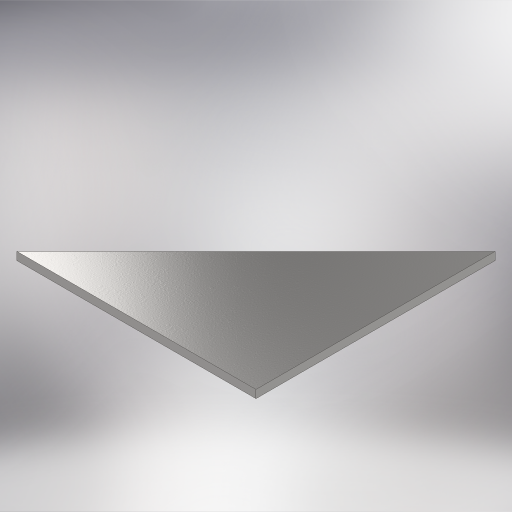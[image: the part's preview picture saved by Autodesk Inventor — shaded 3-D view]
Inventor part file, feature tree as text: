
AUTODESK INVENTOR PART (.ipt)
format: ipt  version: 2023 (Build 270158000, 158)  size: 335,872 bytes
history: native  units: mm
features: other x1, extrude x1, sketch x1
ambient origin geometry x8: Origin, YZ Plane, XZ Plane, XY Plane, X Axis, Y Axis, Z Axis, Center Point
bodies: Body1 (feature_tree)
feature tree (3):
  other  "Sólido1"
  extrude  "Extrusão1"  Depth=3.0mm TaperAngle=0.0deg
  sketch  "Esboço1"  dims[d0=90.0mm d1=3.0mm d2=0.0mm]
